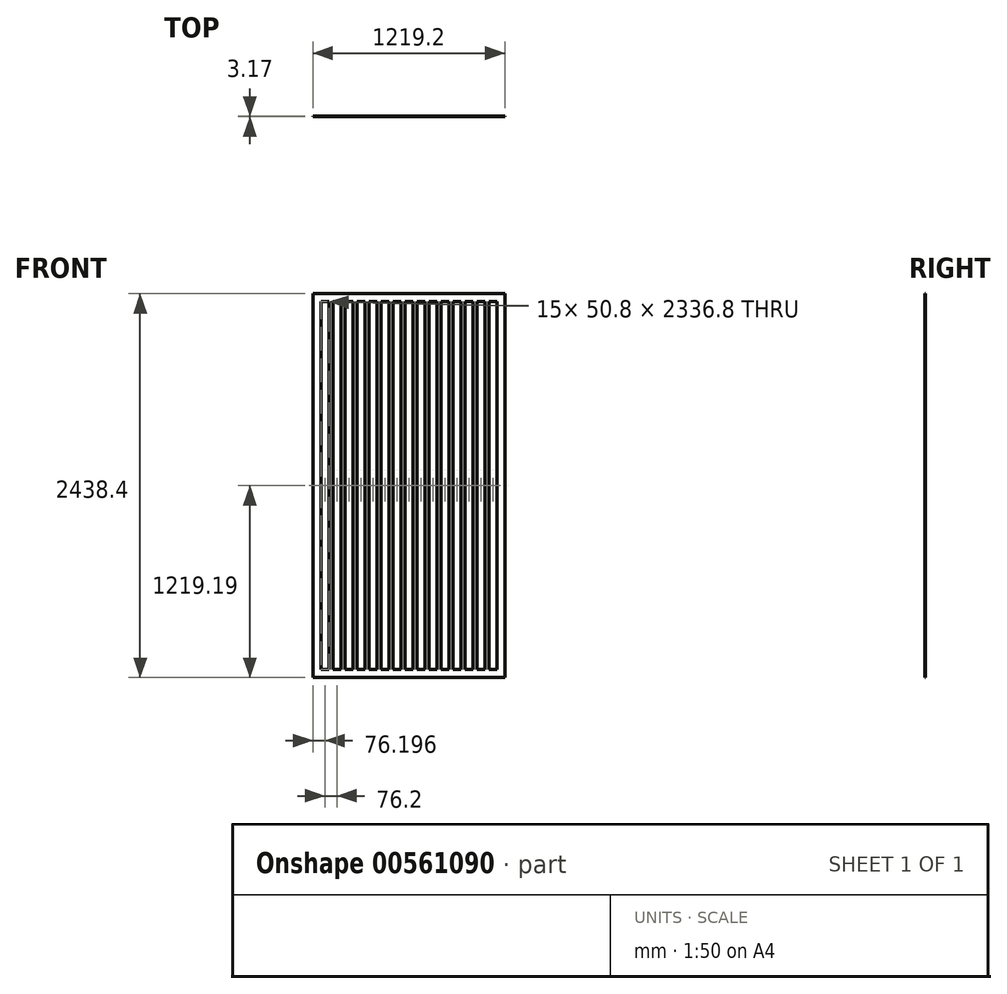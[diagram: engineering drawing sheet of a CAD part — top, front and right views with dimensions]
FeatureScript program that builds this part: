
annotation { "Feature Type Name" : "Feature", "Feature Type Description" : "" }
export const myFeature = defineFeature(function(context is Context, id is Id, definition is map)
    precondition{}
    {
        {
            var Q0;
            Q0=qCreatedBy(makeId("Front.planeOp"),FACE);
            var sketch = newSketch(context, id + "F0", { "sketchPlane" : qUnion([Q0])});
            skLineSegment(sketch, "E0.bottom", {"start": v(-655.55, 972.2) * mm, "end": v(563.65, 972.2) * mm});
            skLineSegment(sketch, "E0.top", {"start": v(-655.55, -1466.2) * mm, "end": v(563.65, -1466.2) * mm});
            skLineSegment(sketch, "E0.left", {"start": v(-655.55, 972.2) * mm, "end": v(-655.55, -1466.2) * mm});
            skLineSegment(sketch, "E1.bottom", {"start": v(-604.75, 921.4) * mm, "end": v(-553.95, 921.4) * mm});
            skLineSegment(sketch, "E1.top", {"start": v(-604.75, -1415.4) * mm, "end": v(-553.95, -1415.4) * mm});
            skLineSegment(sketch, "E1.left", {"start": v(-604.75, 921.4) * mm, "end": v(-604.75, -1415.4) * mm});
            skLineSegment(sketch, "E1.right", {"start": v(-553.95, 921.4) * mm, "end": v(-553.95, -1415.4) * mm});
            skLineSegment(sketch, "E2.1.0.0", {"start": v(-528.55, 921.4) * mm, "end": v(-528.55, -1415.4) * mm});
            skLineSegment(sketch, "E2.1.0.1", {"start": v(-477.75, 921.4) * mm, "end": v(-477.75, -1415.4) * mm});
            skLineSegment(sketch, "E2.1.0.2", {"start": v(-528.55, 921.4) * mm, "end": v(-477.75, 921.4) * mm});
            skLineSegment(sketch, "E2.1.0.3", {"start": v(-528.55, -1415.4) * mm, "end": v(-477.75, -1415.4) * mm});
            skLineSegment(sketch, "E2.2.0.0", {"start": v(-452.35, 921.4) * mm, "end": v(-452.35, -1415.4) * mm});
            skLineSegment(sketch, "E2.2.0.1", {"start": v(-401.55, 921.4) * mm, "end": v(-401.55, -1415.4) * mm});
            skLineSegment(sketch, "E2.2.0.2", {"start": v(-452.35, 921.4) * mm, "end": v(-401.55, 921.4) * mm});
            skLineSegment(sketch, "E2.2.0.3", {"start": v(-452.35, -1415.4) * mm, "end": v(-401.55, -1415.4) * mm});
            skLineSegment(sketch, "E2.3.0.0", {"start": v(-376.15, 921.4) * mm, "end": v(-376.15, -1415.4) * mm});
            skLineSegment(sketch, "E2.3.0.1", {"start": v(-325.35, 921.4) * mm, "end": v(-325.35, -1415.4) * mm});
            skLineSegment(sketch, "E2.3.0.2", {"start": v(-376.15, 921.4) * mm, "end": v(-325.35, 921.4) * mm});
            skLineSegment(sketch, "E2.3.0.3", {"start": v(-376.15, -1415.4) * mm, "end": v(-325.35, -1415.4) * mm});
            skLineSegment(sketch, "E2.4.0.0", {"start": v(-299.95, 921.4) * mm, "end": v(-299.95, -1415.4) * mm});
            skLineSegment(sketch, "E2.4.0.1", {"start": v(-249.15, 921.4) * mm, "end": v(-249.15, -1415.4) * mm});
            skLineSegment(sketch, "E2.4.0.2", {"start": v(-299.95, 921.4) * mm, "end": v(-249.15, 921.4) * mm});
            skLineSegment(sketch, "E2.4.0.3", {"start": v(-299.95, -1415.4) * mm, "end": v(-249.15, -1415.4) * mm});
            skLineSegment(sketch, "E2.5.0.0", {"start": v(-223.75, 921.4) * mm, "end": v(-223.75, -1415.4) * mm});
            skLineSegment(sketch, "E2.5.0.1", {"start": v(-172.95, 921.4) * mm, "end": v(-172.95, -1415.4) * mm});
            skLineSegment(sketch, "E2.5.0.2", {"start": v(-223.75, 921.4) * mm, "end": v(-172.95, 921.4) * mm});
            skLineSegment(sketch, "E2.5.0.3", {"start": v(-223.75, -1415.4) * mm, "end": v(-172.95, -1415.4) * mm});
            skLineSegment(sketch, "E2.6.0.0", {"start": v(-147.55, 921.4) * mm, "end": v(-147.55, -1415.4) * mm});
            skLineSegment(sketch, "E2.6.0.1", {"start": v(-96.75, 921.4) * mm, "end": v(-96.75, -1415.4) * mm});
            skLineSegment(sketch, "E2.6.0.2", {"start": v(-147.55, 921.4) * mm, "end": v(-96.75, 921.4) * mm});
            skLineSegment(sketch, "E2.6.0.3", {"start": v(-147.55, -1415.4) * mm, "end": v(-96.75, -1415.4) * mm});
            skLineSegment(sketch, "E2.7.0.0", {"start": v(-71.35, 921.4) * mm, "end": v(-71.35, -1415.4) * mm});
            skLineSegment(sketch, "E2.7.0.1", {"start": v(-20.55, 921.4) * mm, "end": v(-20.55, -1415.4) * mm});
            skLineSegment(sketch, "E2.7.0.2", {"start": v(-71.35, 921.4) * mm, "end": v(-20.55, 921.4) * mm});
            skLineSegment(sketch, "E2.7.0.3", {"start": v(-71.35, -1415.4) * mm, "end": v(-20.55, -1415.4) * mm});
            skLineSegment(sketch, "E2.8.0.0", {"start": v(4.85, 921.4) * mm, "end": v(4.85, -1415.4) * mm});
            skLineSegment(sketch, "E2.8.0.1", {"start": v(55.65, 921.4) * mm, "end": v(55.65, -1415.4) * mm});
            skLineSegment(sketch, "E2.8.0.2", {"start": v(4.85, 921.4) * mm, "end": v(55.65, 921.4) * mm});
            skLineSegment(sketch, "E2.8.0.3", {"start": v(4.85, -1415.4) * mm, "end": v(55.65, -1415.4) * mm});
            skLineSegment(sketch, "E2.9.0.0", {"start": v(81.05, 921.4) * mm, "end": v(81.05, -1415.4) * mm});
            skLineSegment(sketch, "E2.9.0.1", {"start": v(131.85, 921.4) * mm, "end": v(131.85, -1415.4) * mm});
            skLineSegment(sketch, "E2.9.0.2", {"start": v(81.05, 921.4) * mm, "end": v(131.85, 921.4) * mm});
            skLineSegment(sketch, "E2.9.0.3", {"start": v(81.05, -1415.4) * mm, "end": v(131.85, -1415.4) * mm});
            skLineSegment(sketch, "E2.10.0.0", {"start": v(157.25, 921.4) * mm, "end": v(157.25, -1415.4) * mm});
            skLineSegment(sketch, "E2.10.0.1", {"start": v(208.05, 921.4) * mm, "end": v(208.05, -1415.4) * mm});
            skLineSegment(sketch, "E2.10.0.2", {"start": v(157.25, 921.4) * mm, "end": v(208.05, 921.4) * mm});
            skLineSegment(sketch, "E2.10.0.3", {"start": v(157.25, -1415.4) * mm, "end": v(208.05, -1415.4) * mm});
            skLineSegment(sketch, "E2.11.0.0", {"start": v(233.45, 921.4) * mm, "end": v(233.45, -1415.4) * mm});
            skLineSegment(sketch, "E2.11.0.1", {"start": v(284.25, 921.4) * mm, "end": v(284.25, -1415.4) * mm});
            skLineSegment(sketch, "E2.11.0.2", {"start": v(233.45, 921.4) * mm, "end": v(284.25, 921.4) * mm});
            skLineSegment(sketch, "E2.11.0.3", {"start": v(233.45, -1415.4) * mm, "end": v(284.25, -1415.4) * mm});
            skLineSegment(sketch, "E2.12.0.0", {"start": v(309.65, 921.4) * mm, "end": v(309.65, -1415.4) * mm});
            skLineSegment(sketch, "E2.12.0.1", {"start": v(360.45, 921.4) * mm, "end": v(360.45, -1415.4) * mm});
            skLineSegment(sketch, "E2.12.0.2", {"start": v(309.65, 921.4) * mm, "end": v(360.45, 921.4) * mm});
            skLineSegment(sketch, "E2.12.0.3", {"start": v(309.65, -1415.4) * mm, "end": v(360.45, -1415.4) * mm});
            skLineSegment(sketch, "E2.13.0.0", {"start": v(385.85, 921.4) * mm, "end": v(385.85, -1415.4) * mm});
            skLineSegment(sketch, "E2.13.0.1", {"start": v(436.65, 921.4) * mm, "end": v(436.65, -1415.4) * mm});
            skLineSegment(sketch, "E2.13.0.2", {"start": v(385.85, 921.4) * mm, "end": v(436.65, 921.4) * mm});
            skLineSegment(sketch, "E2.13.0.3", {"start": v(385.85, -1415.4) * mm, "end": v(436.65, -1415.4) * mm});
            skLineSegment(sketch, "E2.14.0.0", {"start": v(462.05, 921.4) * mm, "end": v(462.05, -1415.4) * mm});
            skLineSegment(sketch, "E2.14.0.1", {"start": v(512.85, 921.4) * mm, "end": v(512.85, -1415.4) * mm});
            skLineSegment(sketch, "E2.14.0.2", {"start": v(462.05, 921.4) * mm, "end": v(512.85, 921.4) * mm});
            skLineSegment(sketch, "E2.14.0.3", {"start": v(462.05, -1415.4) * mm, "end": v(512.85, -1415.4) * mm});
            skLineSegment(sketch, "E2.direction1", {"start": v(-604.75, -1415.4) * mm, "end": v(-528.55, -1415.4) * mm, "construction": true});
            skLineSegment(sketch, "E3", {"start": v(563.65, 972.2) * mm, "end": v(563.65, -1466.2) * mm});
            skSolve(sketch);
        }
        {
            var Q0;
            Q0 = qSketchRegion(id + "F0", true);
            extrude(context, id + "F1", {"entities" : qUnion([Q0]), "depth" : 3.17 * mm, "offsetDistance" : 25.4 * mm});
        }
    });
